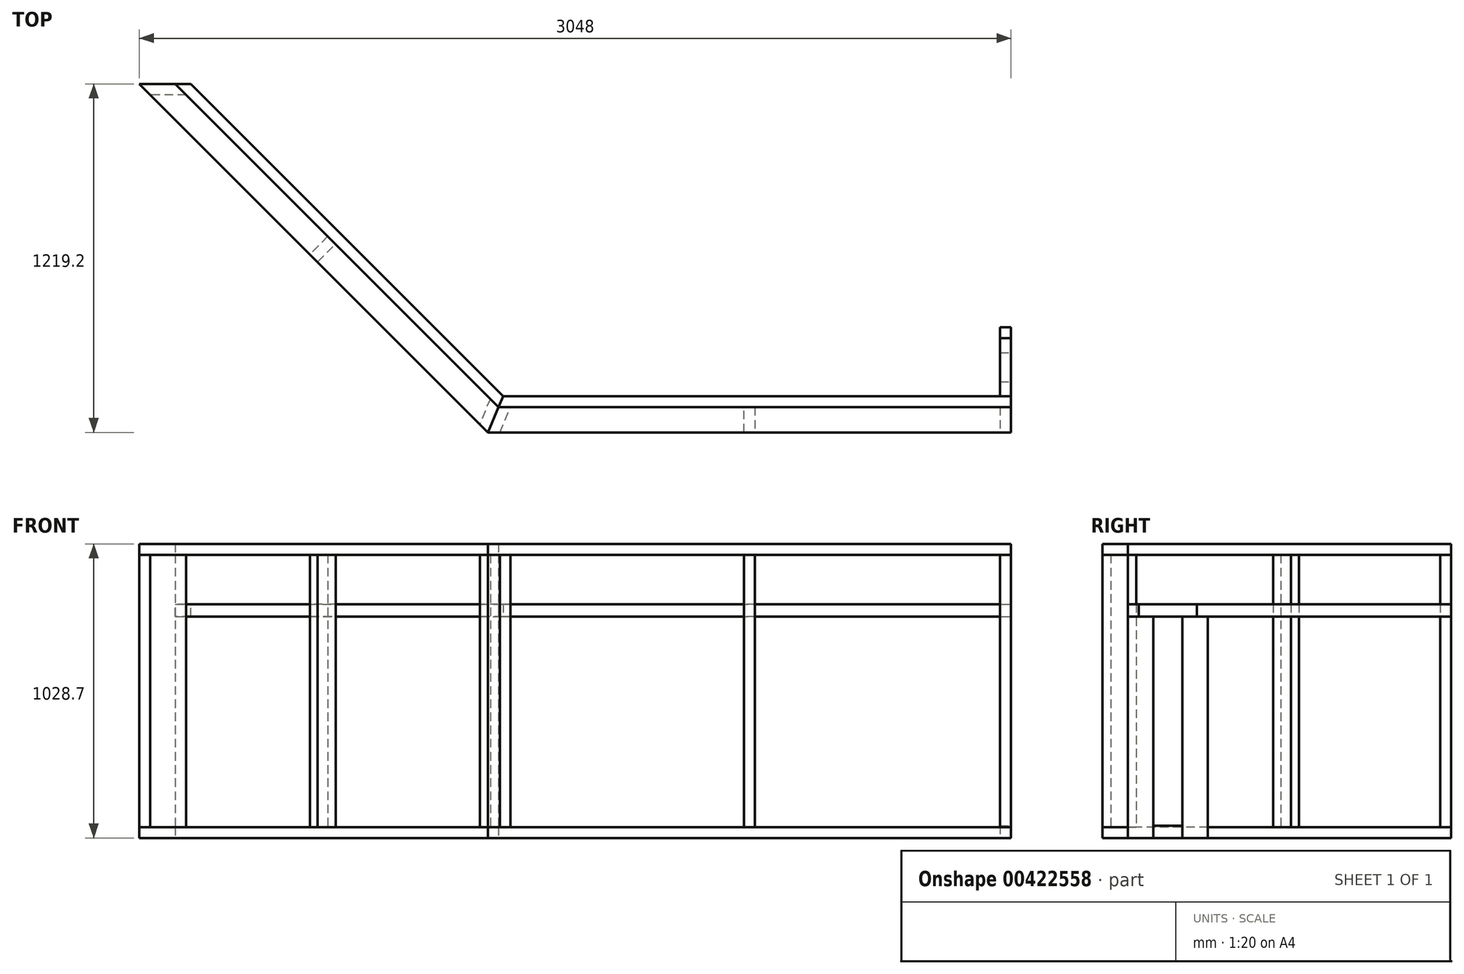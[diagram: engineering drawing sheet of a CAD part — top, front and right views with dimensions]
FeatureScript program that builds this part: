
annotation { "Feature Type Name" : "Feature", "Feature Type Description" : "" }
export const myFeature = defineFeature(function(context is Context, id is Id, definition is map)
    precondition{}
    {
        {
            var Q0;
            Q0=qCreatedBy(makeId("Top.planeOp"),FACE);
            var sketch = newSketch(context, id + "F0", { "sketchPlane" : qUnion([Q0])});
            skLineSegment(sketch, "E0", {"start": v(0, 0) * mm, "end": v(-1791.98, 0) * mm});
            skLineSegment(sketch, "E1", {"start": v(-1791.98, 0) * mm, "end": v(-1828.8, -88.9) * mm});
            skLineSegment(sketch, "E2", {"start": v(-1828.8, -88.9) * mm, "end": v(0, -88.9) * mm});
            skLineSegment(sketch, "E3", {"start": v(0, -88.9) * mm, "end": v(0, 0) * mm});
            skSolve(sketch);
        }
        {
            var Q0;
            Q0=qSketchRegion(id+"F0",true);
            extrude(context, id + "F1", {"entities" : qUnion([Q0]), "depth" : 38.1 * mm});
        }
        {
            var Q0;
            Q0=qCreatedBy(makeId("Top.planeOp"),FACE);
            var sketch = newSketch(context, id + "F2", { "sketchPlane" : qUnion([Q0])});
            skLineSegment(sketch, "E4", {"start": v(-1828.8, -88.9) * mm, "end": v(-3048, 1130.3) * mm});
            skLineSegment(sketch, "E5", {"start": v(-3048, 1130.3) * mm, "end": v(-2922.28, 1130.3) * mm});
            skLineSegment(sketch, "E6", {"start": v(-2922.28, 1130.3) * mm, "end": v(-1791.98, 0) * mm});
            skLineSegment(sketch, "E7", {"start": v(-1828.8, -88.9) * mm, "end": v(-1791.98, 0) * mm});
            skSolve(sketch);
        }
        {
            var Q0;
            Q0=qSketchRegion(id+"F2",true);
            var Q1;
            Q1=makeQuery(id+"F1.opExtrude","CAP_FACE",FACE,{"disambiguationData":[OSD([sQuery(id+"F0.wireOp",EDGE,"E0"),sQuery(id+"F0.wireOp",EDGE,"E1"),sQuery(id+"F0.wireOp",EDGE,"E2"),sQuery(id+"F0.wireOp",EDGE,"E3")])],"isStart":false});
            extrude(context, id + "F3", {"entities" : qUnion([Q0]), "endBound" : BoundingType.UP_TO_SURFACE, "endBoundEntityFace" : qUnion([Q1]), "depth" : 25.4 * mm});
        }
        {
            var Q0;
            Q0=makeQuery(id+"F1.opExtrude","CAP_FACE",FACE,{"disambiguationData":[OSD([sQuery(id+"F0.wireOp",EDGE,"E0"),sQuery(id+"F0.wireOp",EDGE,"E1"),sQuery(id+"F0.wireOp",EDGE,"E2"),sQuery(id+"F0.wireOp",EDGE,"E3")])],"isStart":false});
            var sketch = newSketch(context, id + "F4", { "sketchPlane" : qUnion([Q0])});
            skLineSegment(sketch, "E8", {"start": v(-1828.8, -88.9) * mm, "end": v(-1791.98, 0) * mm});
            skLineSegment(sketch, "E9", {"start": v(-1821.14, 29.16) * mm, "end": v(-1857.96, -59.74) * mm});
            skLineSegment(sketch, "E10", {"start": v(-1857.96, -59.74) * mm, "end": v(-1828.8, -88.9) * mm});
            skLineSegment(sketch, "E11", {"start": v(-1791.98, 0) * mm, "end": v(-1821.14, 29.16) * mm});
            skSolve(sketch);
        }
        {
            var Q0;
            Q0=qSketchRegion(id+"F4",true);
            extrude(context, id + "F5", {"entities" : qUnion([Q0]), "depth" : 952.5 * mm});
        }
        {
            var Q0;
            Q0=makeQuery(id+"F1.opExtrude","CAP_FACE",FACE,{"disambiguationData":[OSD([sQuery(id+"F0.wireOp",EDGE,"E0"),sQuery(id+"F0.wireOp",EDGE,"E1"),sQuery(id+"F0.wireOp",EDGE,"E2"),sQuery(id+"F0.wireOp",EDGE,"E3")])],"isStart":false});
            var sketch = newSketch(context, id + "F6", { "sketchPlane" : qUnion([Q0])});
            skLineSegment(sketch, "E12.bottom", {"start": v(0, 0) * mm, "end": v(-38.1, 0) * mm});
            skLineSegment(sketch, "E12.top", {"start": v(0, -88.9) * mm, "end": v(-38.1, -88.9) * mm});
            skLineSegment(sketch, "E12.left", {"start": v(0, 0) * mm, "end": v(0, -88.9) * mm});
            skLineSegment(sketch, "E12.right", {"start": v(-38.1, 0) * mm, "end": v(-38.1, -88.9) * mm});
            skSolve(sketch);
        }
        {
            var Q0;
            Q0=qSketchRegion(id+"F6",true);
            var Q1;
            Q1=makeQuery(id+"F5.opExtrude","CAP_FACE",FACE,{"disambiguationData":[OSD([sQuery(id+"F4.wireOp",EDGE,"E8"),sQuery(id+"F4.wireOp",EDGE,"riDUiC25-932N-xyHs-kqHV-dJ9bVzyqNV0S"),sQuery(id+"F4.wireOp",EDGE,"E9"),sQuery(id+"F4.wireOp",EDGE,"E10")])],"isStart":false});
            extrude(context, id + "F7", {"entities" : qUnion([Q0]), "endBound" : BoundingType.UP_TO_SURFACE, "endBoundEntityFace" : qUnion([Q1]), "depth" : 25.4 * mm});
        }
        {
            var Q0;
            Q0=makeQuery(id+"F1.opExtrude","CAP_FACE",FACE,{"disambiguationData":[OSD([sQuery(id+"F0.wireOp",EDGE,"E0"),sQuery(id+"F0.wireOp",EDGE,"E1"),sQuery(id+"F0.wireOp",EDGE,"E2"),sQuery(id+"F0.wireOp",EDGE,"E3")])],"isStart":false});
            var sketch = newSketch(context, id + "F8", { "sketchPlane" : qUnion([Q0])});
            skLineSegment(sketch, "E13", {"start": v(-1791.98, 0) * mm, "end": v(-1828.8, -88.9) * mm});
            skLineSegment(sketch, "E14", {"start": v(-1828.8, -88.9) * mm, "end": v(-1787.56, -88.9) * mm});
            skLineSegment(sketch, "E15", {"start": v(-1787.56, -88.9) * mm, "end": v(-1750.74, 0) * mm});
            skLineSegment(sketch, "E16", {"start": v(-1750.74, 0) * mm, "end": v(-1791.98, 0) * mm});
            skSolve(sketch);
        }
        {
            var Q0;
            Q0=qSketchRegion(id+"F8",true);
            var Q1;
            Q1=makeQuery(id+"F5.opExtrude","CAP_FACE",FACE,{"disambiguationData":[OSD([sQuery(id+"F4.wireOp",EDGE,"E8"),sQuery(id+"F4.wireOp",EDGE,"riDUiC25-932N-xyHs-kqHV-dJ9bVzyqNV0S"),sQuery(id+"F4.wireOp",EDGE,"E9"),sQuery(id+"F4.wireOp",EDGE,"E10")])],"isStart":false});
            extrude(context, id + "F9", {"entities" : qUnion([Q0]), "endBound" : BoundingType.UP_TO_SURFACE, "endBoundEntityFace" : qUnion([Q1]), "depth" : 25.4 * mm});
        }
        {
            var Q0;
            Q0=makeQuery(id+"F1.opExtrude","CAP_FACE",FACE,{"disambiguationData":[OSD([sQuery(id+"F0.wireOp",EDGE,"E0"),sQuery(id+"F0.wireOp",EDGE,"E1"),sQuery(id+"F0.wireOp",EDGE,"E2"),sQuery(id+"F0.wireOp",EDGE,"E3")])],"isStart":false});
            var sketch = newSketch(context, id + "F10", { "sketchPlane" : qUnion([Q0])});
            skLineSegment(sketch, "E17", {"start": v(-914.4, -88.9) * mm, "end": v(-895.35, -88.9) * mm});
            skLineSegment(sketch, "E18", {"start": v(-914.4, -88.9) * mm, "end": v(-933.45, -88.9) * mm});
            skLineSegment(sketch, "E19", {"start": v(-933.45, -88.9) * mm, "end": v(-933.45, 0) * mm});
            skLineSegment(sketch, "E20", {"start": v(-933.45, 0) * mm, "end": v(-895.35, 0) * mm});
            skLineSegment(sketch, "E21", {"start": v(-895.35, 0) * mm, "end": v(-895.35, -88.9) * mm});
            skSolve(sketch);
        }
        {
            var Q0;
            Q0=qSketchRegion(id+"F10",true);
            var Q1;
            Q1=makeQuery(id+"F5.opExtrude","CAP_FACE",FACE,{"disambiguationData":[OSD([sQuery(id+"F4.wireOp",EDGE,"E8"),sQuery(id+"F4.wireOp",EDGE,"riDUiC25-932N-xyHs-kqHV-dJ9bVzyqNV0S"),sQuery(id+"F4.wireOp",EDGE,"E9"),sQuery(id+"F4.wireOp",EDGE,"E10")])],"isStart":false});
            extrude(context, id + "F11", {"entities" : qUnion([Q0]), "endBound" : BoundingType.UP_TO_SURFACE, "endBoundEntityFace" : qUnion([Q1]), "depth" : 25.4 * mm});
        }
        {
            var Q0;
            Q0=makeQuery(id+"F9.opExtrude","CAP_FACE",FACE,{"disambiguationData":[OSD([sQuery(id+"F8.wireOp",EDGE,"E13"),sQuery(id+"F8.wireOp",EDGE,"E14"),sQuery(id+"F8.wireOp",EDGE,"E15"),sQuery(id+"F8.wireOp",EDGE,"E16")])],"isStart":false});
            var sketch = newSketch(context, id + "F12", { "sketchPlane" : qUnion([Q0])});
            skLineSegment(sketch, "E22", {"start": v(-1828.8, -88.9) * mm, "end": v(-1791.98, 0) * mm});
            skLineSegment(sketch, "E23", {"start": v(-1791.98, 0) * mm, "end": v(0, 0) * mm});
            skLineSegment(sketch, "E24", {"start": v(0, 0) * mm, "end": v(0, -88.9) * mm});
            skLineSegment(sketch, "E25", {"start": v(0, -88.9) * mm, "end": v(-1828.8, -88.9) * mm});
            skSolve(sketch);
        }
        {
            var Q0;
            Q0=qSketchRegion(id+"F12",true);
            extrude(context, id + "F13", {"entities" : qUnion([Q0]), "depth" : 38.1 * mm});
        }
        {
            var Q0;
            Q0=makeQuery(id+"F3.opExtrude","CAP_FACE",FACE,{"disambiguationData":[OSD([sQuery(id+"F2.wireOp",EDGE,"E4"),sQuery(id+"F2.wireOp",EDGE,"E5"),sQuery(id+"F2.wireOp",EDGE,"E6"),sQuery(id+"F2.wireOp",EDGE,"E7")])],"isStart":false});
            var sketch = newSketch(context, id + "F14", { "sketchPlane" : qUnion([Q0])});
            skLineSegment(sketch, "E26", {"start": v(-3048, 1130.3) * mm, "end": v(-2922.28, 1130.3) * mm});
            skLineSegment(sketch, "E27", {"start": v(-2922.28, 1130.3) * mm, "end": v(-2884.18, 1092.2) * mm});
            skLineSegment(sketch, "E28", {"start": v(-2884.18, 1092.2) * mm, "end": v(-3009.9, 1092.2) * mm});
            skLineSegment(sketch, "E29", {"start": v(-3009.9, 1092.2) * mm, "end": v(-3048, 1130.3) * mm});
            skSolve(sketch);
        }
        {
            var Q0;
            Q0=qSketchRegion(id+"F14",true);
            var Q1;
            Q1=makeQuery(id+"F5.opExtrude","CAP_FACE",FACE,{"disambiguationData":[OSD([sQuery(id+"F4.wireOp",EDGE,"E8"),sQuery(id+"F4.wireOp",EDGE,"riDUiC25-932N-xyHs-kqHV-dJ9bVzyqNV0S"),sQuery(id+"F4.wireOp",EDGE,"E9"),sQuery(id+"F4.wireOp",EDGE,"E10")])],"isStart":false});
            extrude(context, id + "F15", {"entities" : qUnion([Q0]), "endBound" : BoundingType.UP_TO_SURFACE, "endBoundEntityFace" : qUnion([Q1]), "depth" : 25.4 * mm});
        }
        {
            var Q0;
            Q0=makeQuery(id+"F5.opExtrude","CAP_FACE",FACE,{"disambiguationData":[OSD([sQuery(id+"F4.wireOp",EDGE,"E8"),sQuery(id+"F4.wireOp",EDGE,"riDUiC25-932N-xyHs-kqHV-dJ9bVzyqNV0S"),sQuery(id+"F4.wireOp",EDGE,"E9"),sQuery(id+"F4.wireOp",EDGE,"E10")])],"isStart":false});
            var sketch = newSketch(context, id + "F16", { "sketchPlane" : qUnion([Q0])});
            skLineSegment(sketch, "E30", {"start": v(-1828.8, -88.9) * mm, "end": v(-3048, 1130.3) * mm});
            skLineSegment(sketch, "E31", {"start": v(-3048, 1130.3) * mm, "end": v(-2922.28, 1130.3) * mm});
            skLineSegment(sketch, "E32", {"start": v(-2922.28, 1130.3) * mm, "end": v(-1791.98, 0) * mm});
            skLineSegment(sketch, "E33", {"start": v(-1791.98, 0) * mm, "end": v(-1828.8, -88.9) * mm});
            skSolve(sketch);
        }
        {
            var Q0;
            Q0=qSketchRegion(id+"F16",true);
            var Q1;
            Q1=makeQuery(id+"F13.opExtrude","CAP_FACE",FACE,{"disambiguationData":[OSD([sQuery(id+"F12.wireOp",EDGE,"E22"),sQuery(id+"F12.wireOp",EDGE,"E23"),sQuery(id+"F12.wireOp",EDGE,"E24"),sQuery(id+"F12.wireOp",EDGE,"E25")])],"isStart":false});
            extrude(context, id + "F17", {"entities" : qUnion([Q0]), "endBound" : BoundingType.UP_TO_SURFACE, "endBoundEntityFace" : qUnion([Q1]), "depth" : 25.4 * mm});
        }
        {
            var Q0;
            Q0=makeQuery(id+"F3.opExtrude","CAP_FACE",FACE,{"disambiguationData":[OSD([sQuery(id+"F2.wireOp",EDGE,"E4"),sQuery(id+"F2.wireOp",EDGE,"E5"),sQuery(id+"F2.wireOp",EDGE,"E6"),sQuery(id+"F2.wireOp",EDGE,"E7")])],"isStart":false});
            var sketch = newSketch(context, id + "F18", { "sketchPlane" : qUnion([Q0])});
            skLineSegment(sketch, "E34", {"start": v(-2438.4, 520.7) * mm, "end": v(-2424.93, 507.23) * mm});
            skLineSegment(sketch, "E35", {"start": v(-2424.93, 507.23) * mm, "end": v(-2362.07, 570.1) * mm});
            skLineSegment(sketch, "E36", {"start": v(-2362.07, 570.1) * mm, "end": v(-2389, 597.03) * mm});
            skLineSegment(sketch, "E37", {"start": v(-2389, 597.03) * mm, "end": v(-2451.87, 534.17) * mm});
            skLineSegment(sketch, "E38", {"start": v(-2451.87, 534.17) * mm, "end": v(-2438.4, 520.7) * mm});
            skSolve(sketch);
        }
        {
            var Q0;
            Q0=qSketchRegion(id+"F18",true);
            var Q1;
            Q1=makeQuery(id+"F17.opExtrude","CAP_FACE",FACE,{"disambiguationData":[OSD([sQuery(id+"F16.wireOp",EDGE,"E30"),sQuery(id+"F16.wireOp",EDGE,"E31"),sQuery(id+"F16.wireOp",EDGE,"E32"),sQuery(id+"F16.wireOp",EDGE,"E33")])],"isStart":true});
            extrude(context, id + "F19", {"entities" : qUnion([Q0]), "endBound" : BoundingType.UP_TO_SURFACE, "endBoundEntityFace" : qUnion([Q1]), "depth" : 25.4 * mm});
        }
        {
            var Q0;
            Q0=makeQuery(id+"F7.opExtrude","SWEPT_FACE",FACE,{"disambiguationData":[OSD([sQuery(id+"F6.wireOp",EDGE,"E12.left")])]});
            var sketch = newSketch(context, id + "F20", { "sketchPlane" : qUnion([Q0])});
            skLineSegment(sketch, "E39.bottom", {"start": v(0, 0) * mm, "end": v(88.9, 0) * mm});
            skLineSegment(sketch, "E39.top", {"start": v(0, 774.7) * mm, "end": v(88.9, 774.7) * mm});
            skLineSegment(sketch, "E39.left", {"start": v(0, 0) * mm, "end": v(0, 774.7) * mm});
            skLineSegment(sketch, "E39.right", {"start": v(88.9, 0) * mm, "end": v(88.9, 774.7) * mm});
            skSolve(sketch);
        }
        {
            var Q0;
            Q0=qSketchRegion(id+"F20",true);
            var Q1;
            Q1=makeQuery(id+"F7.opExtrude","SWEPT_FACE",FACE,{"disambiguationData":[OSD([sQuery(id+"F6.wireOp",EDGE,"E12.right")])]});
            extrude(context, id + "F21", {"entities" : qUnion([Q0]), "endBound" : BoundingType.UP_TO_SURFACE, "oppositeDirection" : true, "endBoundEntityFace" : qUnion([Q1]), "depth" : 25.4 * mm});
        }
        {
            var Q0;
            Q0=makeQuery(id+"F21.opExtrude","CAP_FACE",FACE,{"disambiguationData":[OSD([sQuery(id+"F20.wireOp",EDGE,"E39.bottom"),sQuery(id+"F20.wireOp",EDGE,"E39.top"),sQuery(id+"F20.wireOp",EDGE,"E39.left"),sQuery(id+"F20.wireOp",EDGE,"E39.right")])],"isStart":true});
            var sketch = newSketch(context, id + "F22", { "sketchPlane" : qUnion([Q0])});
            skLineSegment(sketch, "E40.bottom", {"start": v(88.9, 0) * mm, "end": v(190.5, 0) * mm});
            skLineSegment(sketch, "E40.top", {"start": v(88.9, 42.86) * mm, "end": v(190.5, 42.86) * mm});
            skLineSegment(sketch, "E40.left", {"start": v(88.9, 0) * mm, "end": v(88.9, 42.86) * mm});
            skLineSegment(sketch, "E40.right", {"start": v(190.5, 0) * mm, "end": v(190.5, 42.86) * mm});
            skSolve(sketch);
        }
        {
            var Q0;
            Q0=qSketchRegion(id+"F22",true);
            var Q1;
            Q1=makeQuery(id+"F7.opExtrude","SWEPT_FACE",FACE,{"disambiguationData":[OSD([sQuery(id+"F6.wireOp",EDGE,"E12.right")])]});
            extrude(context, id + "F23", {"entities" : qUnion([Q0]), "endBound" : BoundingType.UP_TO_SURFACE, "oppositeDirection" : true, "endBoundEntityFace" : qUnion([Q1]), "depth" : 25.4 * mm});
        }
        {
            var Q0;
            Q0=qSketchRegion(id+"F22",true);
            var Q1;
            Q1=makeQuery(id+"F21.opExtrude","CAP_FACE",FACE,{"disambiguationData":[OSD([sQuery(id+"F20.wireOp",EDGE,"E39.bottom"),sQuery(id+"F20.wireOp",EDGE,"E39.top"),sQuery(id+"F20.wireOp",EDGE,"E39.left"),sQuery(id+"F20.wireOp",EDGE,"E39.right")])],"isStart":false});
            extrude(context, id + "F24", {"entities" : qUnion([Q0]), "endBound" : BoundingType.UP_TO_SURFACE, "oppositeDirection" : true, "endBoundEntityFace" : qUnion([Q1]), "depth" : 25.4 * mm});
        }
        {
            var Q0;
            Q0=makeQuery(id+"F23.opExtrude","CAP_FACE",FACE,{"disambiguationData":[OSD([sQuery(id+"F22.wireOp",EDGE,"E40.bottom"),sQuery(id+"F22.wireOp",EDGE,"E40.top"),sQuery(id+"F22.wireOp",EDGE,"E40.left"),sQuery(id+"F22.wireOp",EDGE,"E40.right")])],"isStart":true});
            var sketch = newSketch(context, id + "F25", { "sketchPlane" : qUnion([Q0])});
            skLineSegment(sketch, "E41.bottom", {"start": v(190.5, 0) * mm, "end": v(279.4, 0) * mm});
            skLineSegment(sketch, "E41.top", {"start": v(190.5, 774.7) * mm, "end": v(279.4, 774.7) * mm});
            skLineSegment(sketch, "E41.left", {"start": v(190.5, 0) * mm, "end": v(190.5, 774.7) * mm});
            skLineSegment(sketch, "E41.right", {"start": v(279.4, 0) * mm, "end": v(279.4, 774.7) * mm});
            skSolve(sketch);
        }
        {
            var Q0;
            Q0=qSketchRegion(id+"F25",true);
            var Q1;
            Q1=makeQuery(id+"F21.opExtrude","CAP_FACE",FACE,{"disambiguationData":[OSD([sQuery(id+"F20.wireOp",EDGE,"E39.bottom"),sQuery(id+"F20.wireOp",EDGE,"E39.top"),sQuery(id+"F20.wireOp",EDGE,"E39.left"),sQuery(id+"F20.wireOp",EDGE,"E39.right")])],"isStart":false});
            extrude(context, id + "F26", {"entities" : qUnion([Q0]), "endBound" : BoundingType.UP_TO_SURFACE, "oppositeDirection" : true, "endBoundEntityFace" : qUnion([Q1]), "depth" : 25.4 * mm});
        }
        {
            var Q0;
            Q0=makeQuery(id+"F21.opExtrude","SWEPT_FACE",FACE,{"disambiguationData":[OSD([sQuery(id+"F20.wireOp",EDGE,"E39.top")])]});
            var sketch = newSketch(context, id + "F27", { "sketchPlane" : qUnion([Q0])});
            skLineSegment(sketch, "E42", {"start": v(0, 0) * mm, "end": v(-1791.98, 0) * mm});
            skLineSegment(sketch, "E43", {"start": v(-1791.98, 0) * mm, "end": v(-1776.2, 38.1) * mm});
            skLineSegment(sketch, "E44", {"start": v(-1776.2, 38.1) * mm, "end": v(0, 38.1) * mm});
            skLineSegment(sketch, "E45", {"start": v(0, 38.1) * mm, "end": v(0, 0) * mm});
            skSolve(sketch);
        }
        {
            var Q0;
            Q0=qSketchRegion(id+"F27",true);
            extrude(context, id + "F28", {"entities" : qUnion([Q0]), "depth" : 42.86 * mm});
        }
        {
            var Q0;
            Q0=makeQuery(id+"F26.opExtrude","CAP_FACE",FACE,{"disambiguationData":[OSD([sQuery(id+"F25.wireOp",EDGE,"E41.bottom"),sQuery(id+"F25.wireOp",EDGE,"E41.top"),sQuery(id+"F25.wireOp",EDGE,"E41.left"),sQuery(id+"F25.wireOp",EDGE,"E41.right")])],"isStart":true});
            var sketch = newSketch(context, id + "F29", { "sketchPlane" : qUnion([Q0])});
            skLineSegment(sketch, "E46.bottom", {"start": v(38.1, 774.7) * mm, "end": v(241.3, 774.7) * mm});
            skLineSegment(sketch, "E46.top", {"start": v(38.1, 817.56) * mm, "end": v(241.3, 817.56) * mm});
            skLineSegment(sketch, "E46.left", {"start": v(38.1, 774.7) * mm, "end": v(38.1, 817.56) * mm});
            skLineSegment(sketch, "E46.right", {"start": v(241.3, 774.7) * mm, "end": v(241.3, 817.56) * mm});
            skSolve(sketch);
        }
        {
            var Q0;
            Q0=qSketchRegion(id+"F29",true);
            var Q1;
            Q1=makeQuery(id+"F26.opExtrude","CAP_FACE",FACE,{"disambiguationData":[OSD([sQuery(id+"F25.wireOp",EDGE,"E41.bottom"),sQuery(id+"F25.wireOp",EDGE,"E41.top"),sQuery(id+"F25.wireOp",EDGE,"E41.left"),sQuery(id+"F25.wireOp",EDGE,"E41.right")])],"isStart":false});
            extrude(context, id + "F30", {"entities" : qUnion([Q0]), "endBound" : BoundingType.UP_TO_SURFACE, "oppositeDirection" : true, "endBoundEntityFace" : qUnion([Q1]), "depth" : 25.4 * mm});
        }
        {
            var Q0;
            Q0=makeQuery(id+"F28.opExtrude","CAP_FACE",FACE,{"disambiguationData":[OSD([sQuery(id+"F27.wireOp",EDGE,"E42"),sQuery(id+"F27.wireOp",EDGE,"E43"),sQuery(id+"F27.wireOp",EDGE,"E44"),sQuery(id+"F27.wireOp",EDGE,"E45")])],"isStart":false});
            var sketch = newSketch(context, id + "F31", { "sketchPlane" : qUnion([Q0])});
            skLineSegment(sketch, "E47", {"start": v(-1791.98, 0) * mm, "end": v(-2922.28, 1130.3) * mm});
            skLineSegment(sketch, "E48", {"start": v(-2922.28, 1130.3) * mm, "end": v(-2868.4, 1130.3) * mm});
            skLineSegment(sketch, "E49", {"start": v(-2868.4, 1130.3) * mm, "end": v(-1776.2, 38.1) * mm});
            skLineSegment(sketch, "E50", {"start": v(-1776.2, 38.1) * mm, "end": v(-1791.98, 0) * mm});
            skSolve(sketch);
        }
        {
            var Q0;
            Q0=qSketchRegion(id+"F31",true);
            var Q1;
            Q1=makeQuery(id+"F28.opExtrude","CAP_FACE",FACE,{"disambiguationData":[OSD([sQuery(id+"F27.wireOp",EDGE,"E42"),sQuery(id+"F27.wireOp",EDGE,"E43"),sQuery(id+"F27.wireOp",EDGE,"E44"),sQuery(id+"F27.wireOp",EDGE,"E45")])],"isStart":true});
            extrude(context, id + "F32", {"entities" : qUnion([Q0]), "endBound" : BoundingType.UP_TO_SURFACE, "oppositeDirection" : true, "endBoundEntityFace" : qUnion([Q1]), "depth" : 25.4 * mm});
        }
    });
